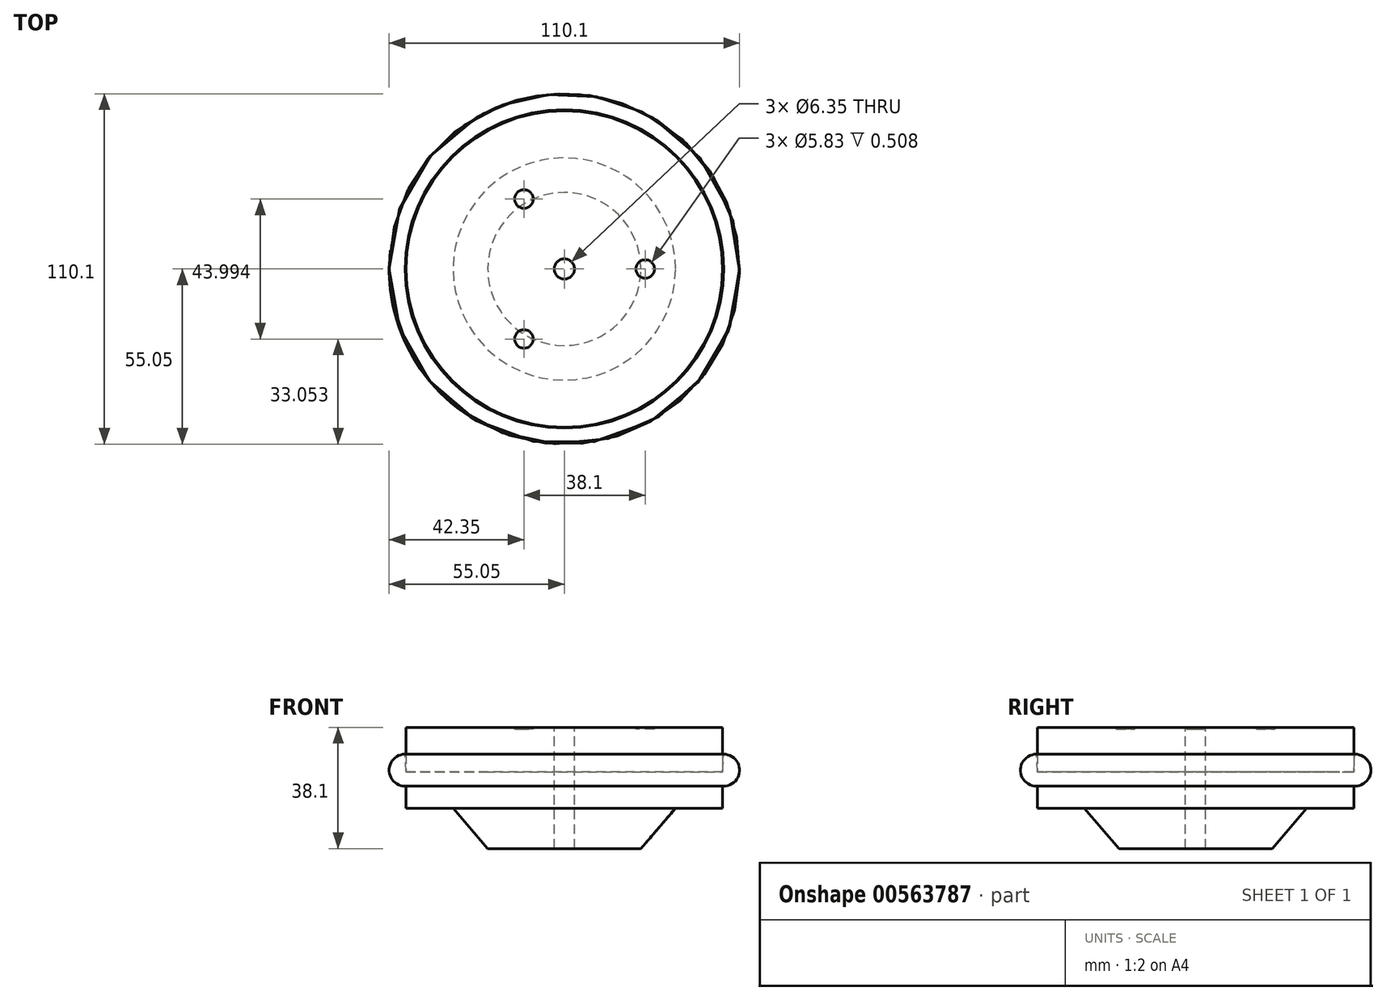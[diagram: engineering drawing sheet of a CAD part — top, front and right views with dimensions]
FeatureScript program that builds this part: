
annotation { "Feature Type Name" : "Feature", "Feature Type Description" : "" }
export const myFeature = defineFeature(function(context is Context, id is Id, definition is map)
    precondition{}
    {
        {
            var Q0;
            Q0=qCreatedBy(makeId("Top.planeOp"),FACE);
            var sketch = newSketch(context, id + "F0", { "sketchPlane" : qUnion([Q0])});
            skCircle(sketch, "E0", {"center": v(0, 0) * mm, "radius": 49.73 * mm});
            skSolve(sketch);
        }
        {
            var Q0;
            Q0 = qSketchRegion(id + "F0", true);
            extrude(context, id + "F1", {"entities" : qUnion([Q0]), "depth" : 25.4 * mm, "offsetDistance" : 25.4 * mm});
        }
        {
            var Q0;
            Q0=qCreatedBy(makeId("Top.planeOp"),FACE);
            var sketch = newSketch(context, id + "F2", { "sketchPlane" : qUnion([Q0])});
            skCircle(sketch, "E1", {"center": v(0, 0) * mm, "radius": 34.93 * mm});
            skSolve(sketch);
        }
        {
            var Q0;
            Q0=qCreatedBy(makeId("Top.planeOp"),FACE);
            cPlane(context, id + "F3", {"entities" : qUnion([Q0]), "cplaneType" : CPlaneType.OFFSET, "offset" : 12.7 * mm, "oppositeDirection" : true, "width" : 152.4 * mm, "height" : 152.4 * mm});
        }
        {
            var Q0;
            Q0=qCreatedBy(id+"F3.planeOp",FACE);
            var sketch = newSketch(context, id + "F4", { "sketchPlane" : qUnion([Q0])});
            skCircle(sketch, "E2", {"center": v(0, 0) * mm, "radius": 24.07 * mm});
            skSolve(sketch);
        }
        {
            var Q1;
            Q1 = qSketchRegion(id + "F4", true);
            var Q2;
            Q2 = qSketchRegion(id + "F2", true);
            loft(context, id + "F5", {"operationType" : NewBodyOperationType.ADD, "sheetProfilesArray" : [{ "sheetProfileEntities" : qUnion([Q1]) }, { "sheetProfileEntities" : qUnion([Q2]) }]});
        }
        {
            var Q0;
            Q0=qCreatedBy(makeId("Front.planeOp"),FACE);
            var sketch = newSketch(context, id + "F6", { "sketchPlane" : qUnion([Q0])});
            skArc(sketch, "E3", {"start": v(-50.04, 16.96) * mm, "mid": v(-55.04, 11.66) * mm, "end": v(-49.48, 6.96) * mm});
            skLineSegment(sketch, "E4", {"start": v(-50.04, 16.96) * mm, "end": v(-49.48, 6.96) * mm});
            skSolve(sketch);
        }
        {
            var Q0;
            Q0 = qSketchRegion(id + "F6", true);
            var Q1;
            Q1=makeQuery(id+"F1.opExtrude","SWEPT_FACE",FACE,{"disambiguationData":[OSD([sQuery(id+"F0.wireOp",EDGE,"E0")])]});
            revolve(context, id + "F7", {"operationType" : NewBodyOperationType.ADD, "entities" : qUnion([Q0]), "axis" : qUnion([Q1]), "revolveType" : RevolveType.FULL});
        }
        {
            var Q0;
            Q0=makeQuery(id+"F1.opExtrude","CAP_FACE",FACE,{"disambiguationData":[OSD([sQuery(id+"F0.wireOp",EDGE,"E0")])],"isStart":false});
            var sketch = newSketch(context, id + "F8", { "sketchPlane" : qUnion([Q0])});
            skCircle(sketch, "E5", {"center": v(0, 0) * mm, "radius": 3.18 * mm});
            skSolve(sketch);
        }
        {
            var Q0;
            Q0 = qSketchRegion(id + "F8", true);
            extrude(context, id + "F9", {"entities" : qUnion([Q0]), "operationType" : NewBodyOperationType.REMOVE, "oppositeDirection" : true, "depth" : 152.4 * mm, "offsetDistance" : 25.4 * mm});
        }
        {
            var Q0;
            Q0=makeQuery(id+"F8.imprint","IMPRINT",FACE,{"disambiguationData":[TD([[makeQuery(id+"F8.imprint","IMPRINT",EDGE,{"derivedFrom":sQuery(id+"F8.wireOp",EDGE,"E5")}),-1.0]])]});
            var sketch = newSketch(context, id + "F10", { "sketchPlane" : qUnion([Q0])});
            skCircle(sketch, "E6", {"center": v(25.4, 0) * mm, "radius": 2.92 * mm});
            skSolve(sketch);
        }
        {
            var Q0;
            Q0 = qSketchRegion(id + "F10", true);
            extrude(context, id + "F11", {"entities" : qUnion([Q0]), "operationType" : NewBodyOperationType.REMOVE, "oppositeDirection" : true, "depth" : 0.5 * mm, "offsetDistance" : 25.4 * mm});
        }
        {
            var Q0;
            Q0=makeQuery(id+"F1.opExtrude","SWEPT_BODY",BODY,{"disambiguationData":[OSD([sQuery(id+"F0.wireOp",EDGE,"E0")])]});
            var Q1;
            Q1=sQuery(id+"F8.wireOp",EDGE,"E5");
            circularPattern(context, id + "F12", {"entities" : qUnion([Q0]), "axis" : qUnion([Q1]), "angle" : 360 * degree, "instanceCount" : 3, "equalSpace" : true});
        }
    });
